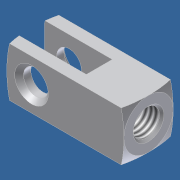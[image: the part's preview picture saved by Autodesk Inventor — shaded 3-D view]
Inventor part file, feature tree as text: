
AUTODESK INVENTOR PART (.ipt)
format: ipt  version: 2012 (Build 160160000, 160)  size: 171,008 bytes
history: native  units: in
note: dims shown in document units (in); Inventor stores cm internally (conversion verified against a paired STEP export)
features: other x126, sketch x7, revolve x5, extrude x2, thread x1
ambient origin geometry x8: Origin, YZ Plane, XZ Plane, XY Plane, X Axis, Y Axis, Z Axis, Center Point
bodies: Solid1 (feature_tree)
feature tree (141):
  extrude  "Extrusion1"  Depth=0.5in TaperAngle=0.0deg
  extrude  "Extrusion2"  Depth=0.44in TaperAngle=0.0deg
  revolve  "Revolution1"  Angle=360.0deg
  thread  "Thread1"  [1 undecoded]
  revolve  "Revolution2"  [1 undecoded]
  revolve  "Revolution3"  [1 undecoded]
  revolve  "Revolution4"  [1 undecoded]
  revolve  "Revolution5"  [1 undecoded]
  other  "th1_XY"
  other  "th1_YZ"
  other  "th1_ZX"
  other  "th1_X"
  other  "th1_Y"
  other  "th1_Z"
  other  "th1_Center"
  other  "th2_XY"
  other  "th2_YZ"
  other  "th2_ZX"
  other  "th2_X"
  other  "th2_Y"
  other  "th2_Z"
  other  "th2_Center"
  other  "rod_clevis_body_XY"
  other  "rod_clevis_body_YZ"
  other  "rod_clevis_body_ZX"
  other  "rod_clevis_body_X"
  other  "rod_clevis_body_Y"
  other  "rod_clevis_body_Z"
  other  "rod_clevis_body_Center"
  other  "piston_rod_clevis_XY"
  other  "piston_rod_clevis_YZ"
  other  "piston_rod_clevis_ZX"
  other  "piston_rod_clevis_X"
  other  "piston_rod_clevis_Y"
  other  "piston_rod_clevis_Z"
  other  "piston_rod_clevis_Center"
  other  "dummy_XY"
  other  "dummy_YZ"
  other  "dummy_ZX"
  other  "dummy_X"
  other  "dummy_Y"
  other  "dummy_Z"
  other  "dummy_Center"
  other  "l11_XY"
  other  "l11_YZ"
  other  "l11_ZX"
  other  "l11_X"
  other  "l11_Y"
  other  "l11_Z"
  other  "l11_Center"
  other  "l12_XY"
  other  "l12_YZ"
  other  "l12_ZX"
  other  "l12_X"
  other  "l12_Y"
  other  "l12_Z"
  other  "l12_Center"
  other  "l1_XY"
  other  "l1_YZ"
  other  "l1_ZX"
  other  "l1_X"
  other  "l1_Y"
  other  "l1_Z"
  other  "l1_Center"
  other  "h1_XY"
  other  "h1_YZ"
  other  "h1_ZX"
  other  "h1_X"
  other  "h1_Y"
  other  "h1_Z"
  other  "h1_Center"
  other  "l2_XY"
  other  "l2_YZ"
  other  "l2_ZX"
  other  "l2_X"
  other  "l2_Y"
  other  "l2_Z"
  other  "l2_Center"
  other  "h2_XY"
  other  "h2_YZ"
  other  "h2_ZX"
  other  "h2_X"
  other  "h2_Y"
  other  "h2_Z"
  other  "h2_Center"
  other  "w11_XY"
  other  "w11_YZ"
  other  "w11_ZX"
  other  "w11_X"
  other  "w11_Y"
  other  "w11_Z"
  other  "w11_Center"
  other  "w12_XY"
  other  "w12_YZ"
  other  "w12_ZX"
  other  "w12_X"
  other  "w12_Y"
  other  "w12_Z"
  other  "w12_Center"
  other  "l21_XY"
  other  "l21_YZ"
  other  "l21_ZX"
  other  "l21_X"
  other  "l21_Y"
  other  "l21_Z"
  other  "l21_Center"
  other  "l22_XY"
  other  "l22_YZ"
  other  "l22_ZX"
  other  "l22_X"
  other  "l22_Y"
  other  "l22_Z"
  other  "l22_Center"
  other  "w1_XY"
  other  "w1_YZ"
  other  "w1_ZX"
  other  "w1_X"
  other  "w1_Y"
  other  "w1_Z"
  other  "w1_Center"
  other  "w2_XY"
  other  "w2_YZ"
  other  "w2_ZX"
  other  "w2_X"
  other  "w2_Y"
  other  "w2_Z"
  other  "w2_Center"
  other  "to_cylinder_XY"
  other  "to_cylinder_YZ"
  other  "to_cylinder_ZX"
  other  "to_cylinder_X"
  other  "to_cylinder_Y"
  other  "to_cylinder_Z"
  other  "to_cylinder_Center"
  sketch  "Sketch_1"  dims[d0=0.5in d1=0.0in d2=0.5in d3=0.0in]
  sketch  "Sketch_2"  dims[d4=360.0deg d5=0.44in d6=0.0in]
  sketch  "Sketch_3"  dims[d7=360.0deg d8=360.0deg d9=360.0deg]
  sketch  "Sketch_4"  dims[d10=360.0deg]
  sketch  "Sketch_5"
  sketch  "Sketch_9"
  sketch  "Sketch_10"
note: 5 required parameter values undecoded (feature->parameter linkage not recoverable at this tier; creation-order binding heuristic only, values carry confidence <= 0.55)
